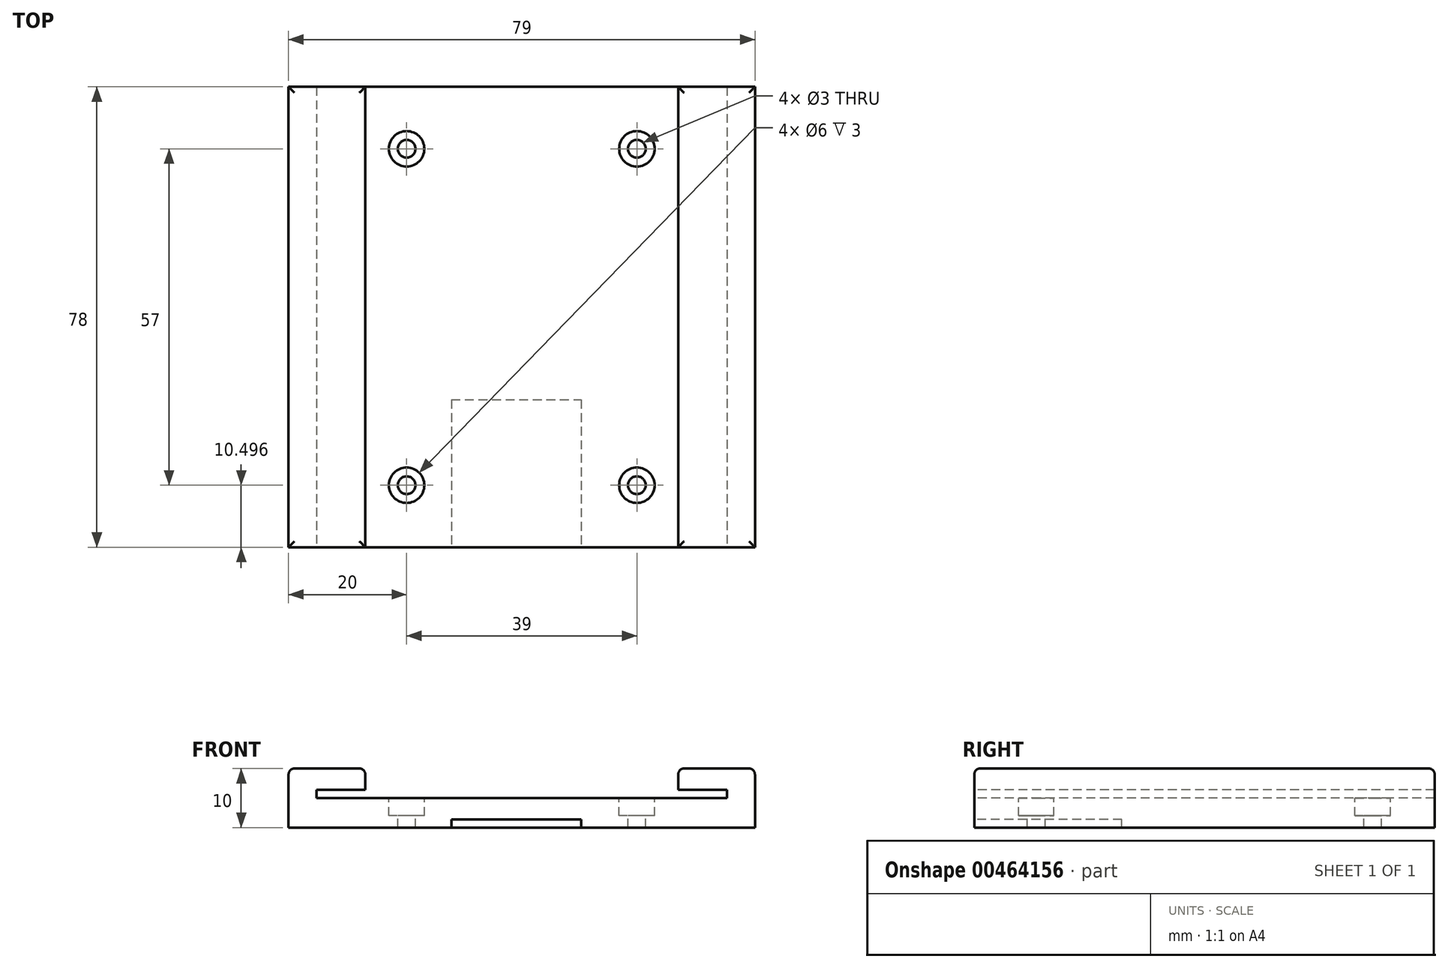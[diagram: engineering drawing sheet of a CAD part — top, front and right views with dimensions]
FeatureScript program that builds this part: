
annotation { "Feature Type Name" : "Feature", "Feature Type Description" : "" }
export const myFeature = defineFeature(function(context is Context, id is Id, definition is map)
    precondition{}
    {
        {
            var Q0;
            Q0=qCreatedBy(makeId("Top.planeOp"),FACE);
            var sketch = newSketch(context, id + "F0", { "sketchPlane" : qUnion([Q0])});
            skLineSegment(sketch, "E0.bottom", {"start": v(-37.22, 48.7) * mm, "end": v(41.78, 48.7) * mm});
            skLineSegment(sketch, "E0.top", {"start": v(-37.22, -29.3) * mm, "end": v(41.78, -29.3) * mm});
            skLineSegment(sketch, "E0.left", {"start": v(-37.22, 48.7) * mm, "end": v(-37.22, -29.3) * mm});
            skLineSegment(sketch, "E0.right", {"start": v(41.78, 48.7) * mm, "end": v(41.78, -29.3) * mm});
            skSolve(sketch);
        }
        {
            var Q0;
            Q0 = qSketchRegion(id + "F0", true);
            extrude(context, id + "F1", {"entities" : qUnion([Q0]), "depth" : 5 * mm});
        }
        {
            var Q0;
            Q0=makeQuery(id+"F1.opExtrude","CAP_FACE",FACE,{"disambiguationData":[OSD([sQuery(id+"F0.wireOp",EDGE,"E0.bottom"),sQuery(id+"F0.wireOp",EDGE,"E0.top"),sQuery(id+"F0.wireOp",EDGE,"E0.left"),sQuery(id+"F0.wireOp",EDGE,"E0.right")])],"isStart":false});
            var sketch = newSketch(context, id + "F2", { "sketchPlane" : qUnion([Q0])});
            skLineSegment(sketch, "E1.bottom", {"start": v(-37.22, 48.7) * mm, "end": v(-24.22, 48.7) * mm});
            skLineSegment(sketch, "E1.top", {"start": v(-37.22, -29.3) * mm, "end": v(-24.22, -29.3) * mm});
            skLineSegment(sketch, "E1.left", {"start": v(-37.22, 48.7) * mm, "end": v(-37.22, -29.3) * mm});
            skLineSegment(sketch, "E1.right", {"start": v(-24.22, 48.7) * mm, "end": v(-24.22, -29.3) * mm});
            skLineSegment(sketch, "E2.bottom", {"start": v(41.78, 48.7) * mm, "end": v(28.78, 48.7) * mm});
            skLineSegment(sketch, "E2.top", {"start": v(41.78, -29.3) * mm, "end": v(28.78, -29.3) * mm});
            skLineSegment(sketch, "E2.left", {"start": v(41.78, 48.7) * mm, "end": v(41.78, -29.3) * mm});
            skLineSegment(sketch, "E2.right", {"start": v(28.78, 48.7) * mm, "end": v(28.78, -29.3) * mm});
            skSolve(sketch);
        }
        {
            var Q0;
            Q0 = qSketchRegion(id + "F2", true);
            extrude(context, id + "F3", {"entities" : qUnion([Q0]), "operationType" : NewBodyOperationType.ADD, "depth" : 5 * mm});
        }
        {
            var Q0;
            Q0=makeQuery(id+"F3.boolean.opBoolean","MERGE",FACE,{"derivedFrom":[makeQuery(id+"F1.opExtrude","SWEPT_FACE",FACE,{"disambiguationData":[OSD([sQuery(id+"F0.wireOp",EDGE,"E0.top")])]}),makeQuery(id+"F3.opExtrude","SWEPT_FACE",FACE,{"disambiguationData":[OSD([sQuery(id+"F2.wireOp",EDGE,"E1.top")])]}),makeQuery(id+"F3.opExtrude","SWEPT_FACE",FACE,{"disambiguationData":[OSD([sQuery(id+"F2.wireOp",EDGE,"E2.top")])]})]});
            var sketch = newSketch(context, id + "F4", { "sketchPlane" : qUnion([Q0])});
            skLineSegment(sketch, "E3.bottom", {"start": v(-24.22, 5) * mm, "end": v(-32.47, 5) * mm});
            skLineSegment(sketch, "E3.top", {"start": v(-24.22, 6.4) * mm, "end": v(-32.47, 6.4) * mm});
            skLineSegment(sketch, "E3.left", {"start": v(-24.22, 5) * mm, "end": v(-24.22, 6.4) * mm});
            skLineSegment(sketch, "E3.right", {"start": v(-32.47, 5) * mm, "end": v(-32.47, 6.4) * mm});
            skLineSegment(sketch, "E4.bottom", {"start": v(28.78, 5) * mm, "end": v(37.03, 5) * mm});
            skLineSegment(sketch, "E4.top", {"start": v(28.78, 6.4) * mm, "end": v(37.03, 6.4) * mm});
            skLineSegment(sketch, "E4.left", {"start": v(28.78, 5) * mm, "end": v(28.78, 6.4) * mm});
            skLineSegment(sketch, "E4.right", {"start": v(37.03, 5) * mm, "end": v(37.03, 6.4) * mm});
            skSolve(sketch);
        }
        {
            var Q0;
            Q0 = qSketchRegion(id + "F4", true);
            extrude(context, id + "F5", {"entities" : qUnion([Q0]), "operationType" : NewBodyOperationType.REMOVE, "endBound" : BoundingType.THROUGH_ALL, "oppositeDirection" : true, "depth" : 25 * mm});
        }
        {
            var Q0;
            Q0=makeQuery(id+"F5.boolean.opBoolean","MERGE",FACE,{"derivedFrom":[makeQuery(id+"F1.opExtrude","CAP_FACE",FACE,{"disambiguationData":[OSD([sQuery(id+"F0.wireOp",EDGE,"E0.bottom"),sQuery(id+"F0.wireOp",EDGE,"E0.top"),sQuery(id+"F0.wireOp",EDGE,"E0.left"),sQuery(id+"F0.wireOp",EDGE,"E0.right")])],"isStart":false}),makeQuery(id+"F5.opExtrude","SWEPT_FACE",FACE,{"disambiguationData":[OSD([sQuery(id+"F4.wireOp",EDGE,"E3.bottom")])]}),makeQuery(id+"F5.opExtrude","SWEPT_FACE",FACE,{"disambiguationData":[OSD([sQuery(id+"F4.wireOp",EDGE,"E4.bottom")])]})]});
            var sketch = newSketch(context, id + "F6", { "sketchPlane" : qUnion([Q0])});
            skCircle(sketch, "E5", {"center": v(-17.22, 38.2) * mm, "radius": 1.5 * mm});
            skCircle(sketch, "E6", {"center": v(21.78, 38.2) * mm, "radius": 1.5 * mm});
            skCircle(sketch, "E7", {"center": v(-17.22, -18.8) * mm, "radius": 1.5 * mm});
            skCircle(sketch, "E8", {"center": v(21.78, -18.8) * mm, "radius": 1.5 * mm});
            skSolve(sketch);
        }
        {
            var Q0;
            Q0 = qSketchRegion(id + "F6", true);
            extrude(context, id + "F7", {"entities" : qUnion([Q0]), "operationType" : NewBodyOperationType.REMOVE, "oppositeDirection" : true, "depth" : 30 * mm});
        }
        {
            var Q0;
            Q0=makeQuery(id+"F5.boolean.opBoolean","MERGE",FACE,{"derivedFrom":[makeQuery(id+"F1.opExtrude","CAP_FACE",FACE,{"disambiguationData":[OSD([sQuery(id+"F0.wireOp",EDGE,"E0.bottom"),sQuery(id+"F0.wireOp",EDGE,"E0.top"),sQuery(id+"F0.wireOp",EDGE,"E0.left"),sQuery(id+"F0.wireOp",EDGE,"E0.right")])],"isStart":false}),makeQuery(id+"F5.opExtrude","SWEPT_FACE",FACE,{"disambiguationData":[OSD([sQuery(id+"F4.wireOp",EDGE,"E3.bottom")])]}),makeQuery(id+"F5.opExtrude","SWEPT_FACE",FACE,{"disambiguationData":[OSD([sQuery(id+"F4.wireOp",EDGE,"E4.bottom")])]})]});
            var sketch = newSketch(context, id + "F8", { "sketchPlane" : qUnion([Q0])});
            skCircle(sketch, "E9", {"center": v(-17.22, 38.2) * mm, "radius": 3 * mm});
            skCircle(sketch, "E10", {"center": v(21.78, 38.2) * mm, "radius": 3 * mm});
            skCircle(sketch, "E11", {"center": v(-17.22, -18.8) * mm, "radius": 3 * mm});
            skCircle(sketch, "E12", {"center": v(21.78, -18.8) * mm, "radius": 3 * mm});
            skSolve(sketch);
        }
        {
            var Q0;
            Q0 = qSketchRegion(id + "F8", true);
            extrude(context, id + "F9", {"entities" : qUnion([Q0]), "operationType" : NewBodyOperationType.REMOVE, "oppositeDirection" : true, "depth" : 3 * mm});
        }
        {
            var Q0;
            Q0=makeQuery(id+"F3.boolean.opBoolean","MERGE",FACE,{"derivedFrom":[makeQuery(id+"F1.opExtrude","SWEPT_FACE",FACE,{"disambiguationData":[OSD([sQuery(id+"F0.wireOp",EDGE,"E0.top")])]}),makeQuery(id+"F3.opExtrude","SWEPT_FACE",FACE,{"disambiguationData":[OSD([sQuery(id+"F2.wireOp",EDGE,"E1.top")])]}),makeQuery(id+"F3.opExtrude","SWEPT_FACE",FACE,{"disambiguationData":[OSD([sQuery(id+"F2.wireOp",EDGE,"E2.top")])]})]});
            var sketch = newSketch(context, id + "F10", { "sketchPlane" : qUnion([Q0])});
            skLineSegment(sketch, "E13.bottom", {"start": v(-9.64, 0) * mm, "end": v(12.36, 0) * mm});
            skLineSegment(sketch, "E13.top", {"start": v(-9.64, 1.4) * mm, "end": v(12.36, 1.4) * mm});
            skLineSegment(sketch, "E13.left", {"start": v(-9.64, 0) * mm, "end": v(-9.64, 1.4) * mm});
            skLineSegment(sketch, "E13.right", {"start": v(12.36, 0) * mm, "end": v(12.36, 1.4) * mm});
            skSolve(sketch);
        }
        {
            var Q0;
            Q0 = qSketchRegion(id + "F10", true);
            extrude(context, id + "F11", {"entities" : qUnion([Q0]), "operationType" : NewBodyOperationType.REMOVE, "oppositeDirection" : true, "depth" : 25 * mm});
        }
        {
            var Q0;
            Q0=makeQuery(id+"F3.opExtrude","CAP_EDGE",EDGE,{"disambiguationData":[OSD([sQuery(id+"F2.wireOp",EDGE,"E1.right")])],"isStart":false});
            var Q1;
            Q1=makeQuery(id+"F3.opExtrude","CAP_EDGE",EDGE,{"disambiguationData":[OSD([sQuery(id+"F2.wireOp",EDGE,"E2.right")])],"isStart":false});
            var Q2;
            Q2=makeQuery(id+"F3.opExtrude","CAP_EDGE",EDGE,{"disambiguationData":[OSD([sQuery(id+"F2.wireOp",EDGE,"E2.top")])],"isStart":false});
            var Q3;
            Q3=makeQuery(id+"F3.opExtrude","CAP_EDGE",EDGE,{"disambiguationData":[OSD([sQuery(id+"F2.wireOp",EDGE,"E1.top")])],"isStart":false});
            var Q4;
            Q4=makeQuery(id+"F3.opExtrude","CAP_EDGE",EDGE,{"disambiguationData":[OSD([sQuery(id+"F2.wireOp",EDGE,"E1.bottom")])],"isStart":false});
            var Q5;
            Q5=makeQuery(id+"F3.opExtrude","CAP_EDGE",EDGE,{"disambiguationData":[OSD([sQuery(id+"F2.wireOp",EDGE,"E2.bottom")])],"isStart":false});
            var Q6;
            Q6=makeQuery(id+"F5.boolean.opBoolean","COPY",EDGE,{"derivedFrom":makeQuery(id+"F5.opExtrude","CAP_EDGE",EDGE,{"disambiguationData":[OSD([sQuery(id+"F4.wireOp",EDGE,"E4.top")])],"isStart":true})});
            var Q7;
            Q7=makeQuery(id+"F5.boolean.opBoolean","COPY",EDGE,{"derivedFrom":makeQuery(id+"F5.opExtrude","CAP_EDGE",EDGE,{"disambiguationData":[OSD([sQuery(id+"F4.wireOp",EDGE,"E3.top")])],"isStart":true})});
            var Q8;
            Q8=makeQuery(id+"F3.opExtrude","CAP_EDGE",EDGE,{"disambiguationData":[OSD([sQuery(id+"F2.wireOp",EDGE,"E2.left")])],"isStart":false});
            var Q9;
            Q9=makeQuery(id+"F3.opExtrude","CAP_EDGE",EDGE,{"disambiguationData":[OSD([sQuery(id+"F2.wireOp",EDGE,"E1.left")])],"isStart":false});
            fillet(context, id + "F12", {"entities" : qUnion([Q0, Q1, Q2, Q3, Q4, Q5, Q6, Q7, Q8, Q9]), "radius" : 1 * mm, "tangentPropagation" : true, "allowEdgeOverflow" : false});
        }
    });
